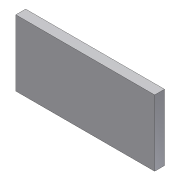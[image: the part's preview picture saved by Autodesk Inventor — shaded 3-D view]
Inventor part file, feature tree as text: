
AUTODESK INVENTOR PART (.ipt)
format: ipt  version: unknown  size: 159,232 bytes
history: native  units: mm (DEFAULTED — no unit token found)
features: extrude x1, sketch x1
ambient origin geometry x8: Origin, YZ Plane, XZ Plane, XY Plane, X Axis, Y Axis, Z Axis, Center Point
feature tree (2):
  extrude  "Extrusion1"  Depth=15.875mm
  sketch  "Sketch1"  dims[d0=33.3375mm d1=15.875mm d2=2.3622mm d3=0.0mm]
